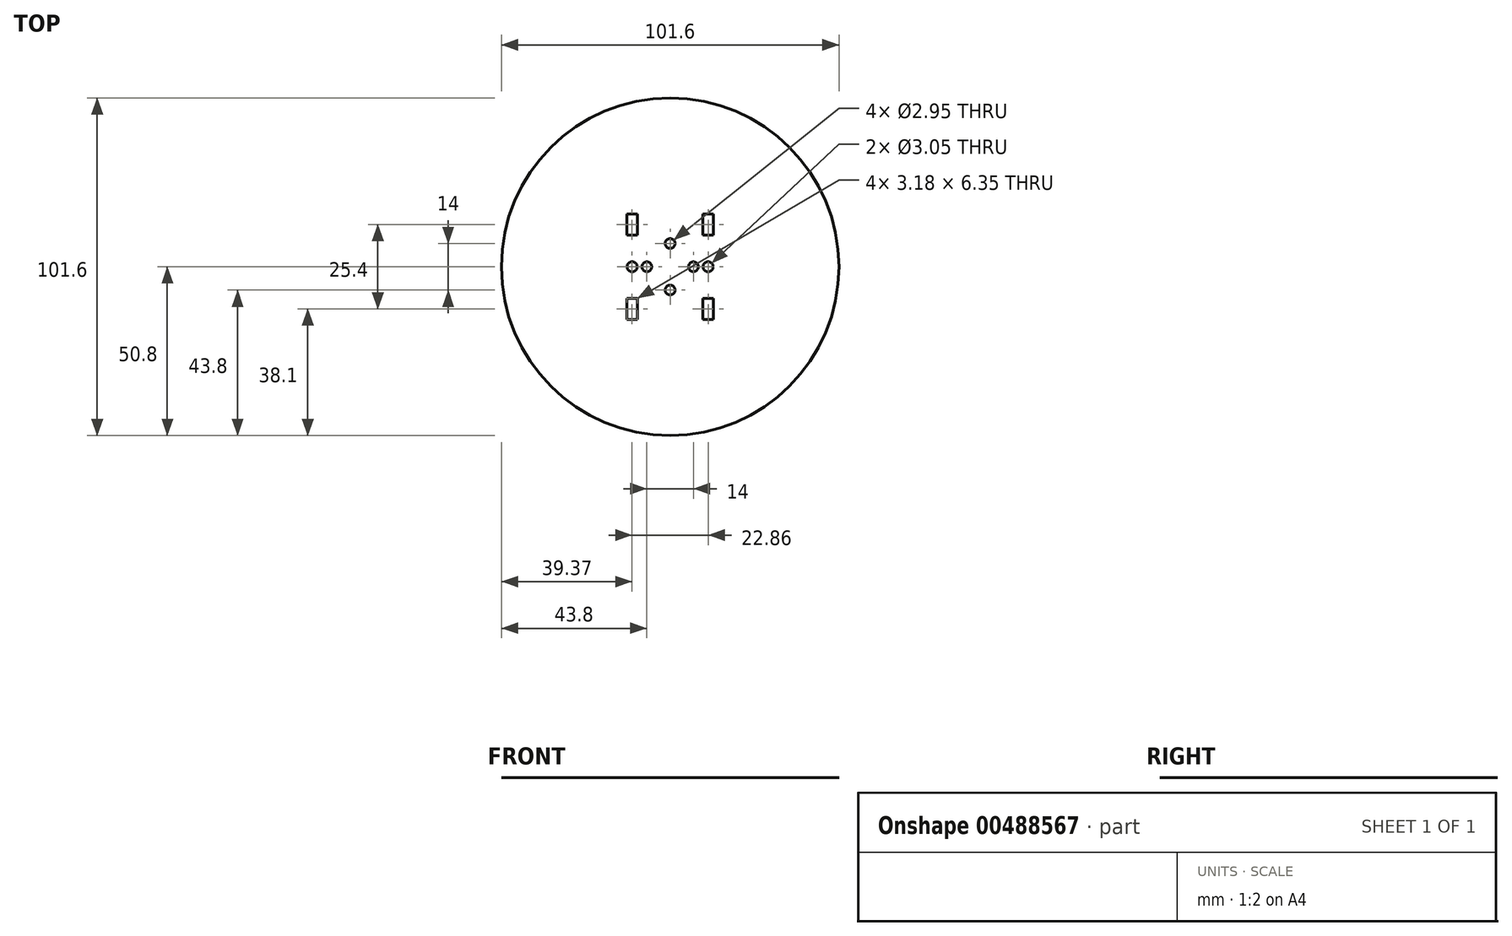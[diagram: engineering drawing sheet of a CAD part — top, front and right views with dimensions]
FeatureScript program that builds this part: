
annotation { "Feature Type Name" : "Feature", "Feature Type Description" : "" }
export const myFeature = defineFeature(function(context is Context, id is Id, definition is map)
    precondition{}
    {
        {
            var Q0;
            Q0=qCreatedBy(makeId("Top.planeOp"),FACE);
            var sketch = newSketch(context, id + "F0", { "sketchPlane" : qUnion([Q0])});
            skCircle(sketch, "E0", {"center": v(0, 0) * mm, "radius": 50.8 * mm});
            skCircle(sketch, "E1", {"center": v(0, 0) * mm, "radius": 7 * mm, "construction": true});
            skCircle(sketch, "E2", {"center": v(0, 7) * mm, "radius": 1.47 * mm});
            skCircle(sketch, "E3", {"center": v(0, -7) * mm, "radius": 1.47 * mm});
            skCircle(sketch, "E4", {"center": v(7, 0) * mm, "radius": 1.47 * mm});
            skCircle(sketch, "E5", {"center": v(-7, 0) * mm, "radius": 1.47 * mm});
            skLineSegment(sketch, "E6", {"start": v(0, 0) * mm, "end": v(11.43, 0) * mm, "construction": true});
            skLineSegment(sketch, "E7", {"start": v(11.43, 0) * mm, "end": v(11.43, 12.7) * mm, "construction": true});
            skLineSegment(sketch, "E8.bottom", {"start": v(13.02, 9.53) * mm, "end": v(9.84, 9.53) * mm});
            skLineSegment(sketch, "E8.top", {"start": v(13.02, 15.88) * mm, "end": v(9.84, 15.88) * mm});
            skLineSegment(sketch, "E8.left", {"start": v(13.02, 9.53) * mm, "end": v(13.02, 15.88) * mm});
            skLineSegment(sketch, "E8.right", {"start": v(9.84, 9.53) * mm, "end": v(9.84, 15.88) * mm});
            skPoint(sketch, "E8.middle", {"position": v(11.43, 12.7) * mm});
            skLineSegment(sketch, "E9.MirrorCS", {"start": v(13.02, -15.88) * mm, "end": v(9.84, -15.88) * mm});
            skLineSegment(sketch, "E10.MirrorCS", {"start": v(9.84, -9.53) * mm, "end": v(9.84, -15.88) * mm});
            skLineSegment(sketch, "E11.MirrorCS", {"start": v(11.43, 0) * mm, "end": v(11.43, -12.7) * mm, "construction": true});
            skLineSegment(sketch, "E12.MirrorCS", {"start": v(13.02, -9.53) * mm, "end": v(9.84, -9.53) * mm});
            skLineSegment(sketch, "E13.MirrorCS", {"start": v(13.02, -9.53) * mm, "end": v(13.02, -15.88) * mm});
            skLineSegment(sketch, "E14.MirrorCS", {"start": v(-9.84, 9.53) * mm, "end": v(-9.84, 15.88) * mm});
            skLineSegment(sketch, "E15.MirrorCS", {"start": v(-13.02, 15.88) * mm, "end": v(-9.84, 15.88) * mm});
            skLineSegment(sketch, "E16.MirrorCS", {"start": v(-13.02, 9.53) * mm, "end": v(-13.02, 15.88) * mm});
            skLineSegment(sketch, "E17.MirrorCS", {"start": v(-11.43, 0) * mm, "end": v(-11.43, 12.7) * mm, "construction": true});
            skLineSegment(sketch, "E18.MirrorCS", {"start": v(-13.02, 9.53) * mm, "end": v(-9.84, 9.53) * mm});
            skLineSegment(sketch, "E19.MirrorCS", {"start": v(-13.02, -9.53) * mm, "end": v(-9.84, -9.53) * mm});
            skLineSegment(sketch, "E20.MirrorCS", {"start": v(-13.02, -9.53) * mm, "end": v(-13.02, -15.88) * mm});
            skLineSegment(sketch, "E21.MirrorCS", {"start": v(-13.02, -15.88) * mm, "end": v(-9.84, -15.88) * mm});
            skLineSegment(sketch, "E22.MirrorCS", {"start": v(-9.84, -9.53) * mm, "end": v(-9.84, -15.88) * mm});
            skCircle(sketch, "E23", {"center": v(11.43, 0) * mm, "radius": 1.52 * mm});
            skCircle(sketch, "E24.MirrorC", {"center": v(-11.43, 0) * mm, "radius": 1.52 * mm});
            skSolve(sketch);
        }
        {
            var Q0;
            Q0=makeQuery(id+"F0.imprint","IMPRINT",FACE,{"disambiguationData":[TD([[makeQuery(id+"F0.imprint","IMPRINT",EDGE,{"derivedFrom":sQuery(id+"F0.wireOp",EDGE,"E0")}),1.0]])]});
            extrude(context, id + "F1", {"entities" : qUnion([Q0]), "depth" : 1 / 203.2 * mm});
        }
    });
